annotation { "Feature Type Name" : "Feature", "Feature Type Description" : "" }
export const myFeature = defineFeature(function(context is Context, id is Id, definition is map)
    precondition{}
    {
        {
            var Q0;
            Q0=qCreatedBy(makeId("Top.planeOp"),FACE);
            var sketch = newSketch(context, id + "F0", { "sketchPlane" : qUnion([Q0])});
            skCircle(sketch, "E0", {"center": v(-73, 0) * mm, "radius": 6.75 * mm});
            skArc(sketch, "E1", {"start": v(-66, 9.75) * mm, "mid": v(-85, 0) * mm, "end": v(-66, -9.75) * mm});
            skLineSegment(sketch, "E2", {"start": v(0, 7.5) * mm, "end": v(-59, 7.5) * mm});
            skLineSegment(sketch, "E3", {"start": v(-59, -7.5) * mm, "end": v(0, -7.5) * mm});
            skLineSegment(sketch, "E4", {"start": v(-73, 0) * mm, "end": v(0, 0) * mm, "construction": true});
            skLineSegment(sketch, "E5", {"start": v(0, 0) * mm, "end": v(0, 32.48) * mm, "construction": true});
            skPoint(sketch, "E6.visualSharp", {"position": v(-63.63, 7.5) * mm});
            skArc(sketch, "E6.filletArc", {"start": v(-66, 9.75) * mm, "mid": v(-62.68, 8.08) * mm, "end": v(-59, 7.5) * mm});
            skPoint(sketch, "E7.visualSharp", {"position": v(-63.63, -7.5) * mm});
            skArc(sketch, "E7.filletArc", {"start": v(-59, -7.5) * mm, "mid": v(-62.68, -8.08) * mm, "end": v(-66, -9.75) * mm});
            skLineSegment(sketch, "E8.0.MirrorCS", {"start": v(0, 7.5) * mm, "end": v(59, 7.5) * mm});
            skLineSegment(sketch, "E9.0.MirrorCS", {"start": v(59, -7.5) * mm, "end": v(0, -7.5) * mm});
            skArc(sketch, "E10.0.MirrorCS", {"start": v(59, -7.5) * mm, "mid": v(62.68, -8.08) * mm, "end": v(66, -9.75) * mm});
            skArc(sketch, "E11.0.MirrorCS", {"start": v(66, 9.75) * mm, "mid": v(62.68, 8.08) * mm, "end": v(59, 7.5) * mm});
            skArc(sketch, "E12.0.MirrorCS", {"start": v(66, 9.75) * mm, "mid": v(85, 0) * mm, "end": v(66, -9.75) * mm});
            skCircle(sketch, "E13.0.MirrorC", {"center": v(73, 0) * mm, "radius": 6.75 * mm});
            skLineSegment(sketch, "E14", {"start": v(-89.97, 0) * mm, "end": v(0, 89.97) * mm, "construction": true});
            skLineSegment(sketch, "E15", {"start": v(0, 89.97) * mm, "end": v(89.97, 0) * mm, "construction": true});
            skLineSegment(sketch, "E16", {"start": v(89.97, 0) * mm, "end": v(0, -89.97) * mm, "construction": true});
            skLineSegment(sketch, "E17", {"start": v(0, -89.97) * mm, "end": v(-89.97, 0) * mm, "construction": true});
            skSolve(sketch);
        }
        {
            var Q0;
            Q0=qSketchRegion(id+"F0",true);
            extrude(context, id + "F1", {"entities" : qUnion([Q0]), "depth" : 3 * mm});
        }
        {
            var Q0;
            Q0=makeQuery(id+"F1.opExtrude","CAP_FACE",FACE,{"disambiguationData":[OSD([sQuery(id+"F0.wireOp",EDGE,"E0"),sQuery(id+"F0.wireOp",EDGE,"E1"),sQuery(id+"F0.wireOp",EDGE,"E2"),sQuery(id+"F0.wireOp",EDGE,"E3"),sQuery(id+"F0.wireOp",EDGE,"E6.filletArc"),sQuery(id+"F0.wireOp",EDGE,"E7.filletArc"),sQuery(id+"F0.wireOp",EDGE,"E8.0.MirrorCS"),sQuery(id+"F0.wireOp",EDGE,"E9.0.MirrorCS"),sQuery(id+"F0.wireOp",EDGE,"E10.0.MirrorCS"),sQuery(id+"F0.wireOp",EDGE,"E11.0.MirrorCS"),sQuery(id+"F0.wireOp",EDGE,"E12.0.MirrorCS"),sQuery(id+"F0.wireOp",EDGE,"E13.0.MirrorC")])],"isStart":false});
            var sketch = newSketch(context, id + "F2", { "sketchPlane" : qUnion([Q0])});
            skLineSegment(sketch, "E18", {"start": v(0, 0) * mm, "end": v(0, 28.86) * mm, "construction": true});
            skLineSegment(sketch, "E19", {"start": v(0, 0) * mm, "end": v(61.74, 0) * mm, "construction": true});
            skText(sketch, "E20", { "text": "DRAGON MOUNTAIN", "fontName": "NotoSansCJKsc-Bold.otf"});
            const initialGuessF2  = {"E20": [-0.05, -0.00365, 1, 0, 0.0073]};
            skSetInitialGuess(sketch, initialGuessF2);
            skSolve(sketch);
        }
        {
            var Q0;
            Q0=qSketchRegion(id+"F2",true);
            extrude(context, id + "F3", {"entities" : qUnion([Q0]), "operationType" : NewBodyOperationType.ADD, "depth" : 0.5 * mm});
        }
        {
            var Q0;
            Q0=makeQuery(id+"F1.opExtrude","CAP_EDGE",EDGE,{"disambiguationData":[OSD([sQuery(id+"F0.wireOp",EDGE,"E3"),sQuery(id+"F0.wireOp",EDGE,"E9.0.MirrorCS")])],"isStart":false});
            fillet(context, id + "F4", {"entities" : qUnion([Q0]), "radius" : 1 * mm, "tangentPropagation" : true, "allowEdgeOverflow" : false});
        }
    });